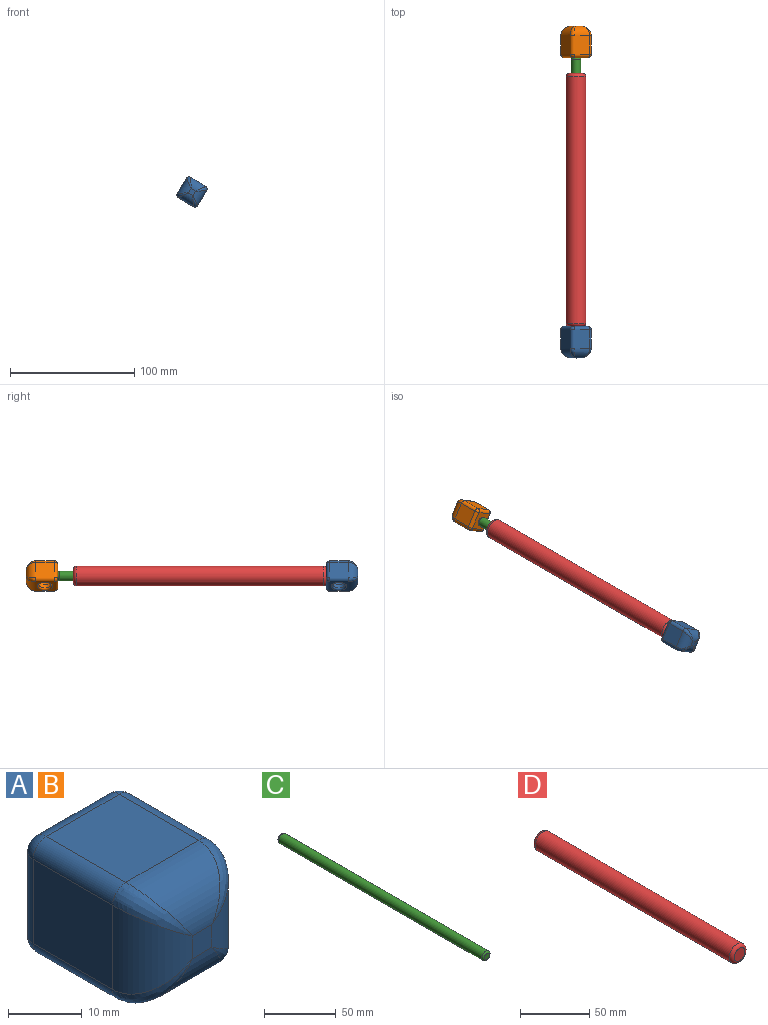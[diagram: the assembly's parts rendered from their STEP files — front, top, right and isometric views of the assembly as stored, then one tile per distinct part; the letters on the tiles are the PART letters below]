
ASSEMBLY  parts=4 mates=6
PART A: 29 faces, bbox 19.1x25.4x19.1 mm
  f0: plane 15.24x13.97mm, normal (0,0,-1), area 212.9mm2, adj f11,f15,f17,f23
  f1: plane 15.24x13.97mm, normal (1,0,0), area 86.2mm2, adj f8,f14,f17,f24,f27
  f2: plane 15.24x13.97mm, normal (0,0,1), area 212.9mm2, adj f6,f8,f9,f20
  f3: plane 15.24x13.97mm, normal (-1,0,0), area 212.9mm2, adj f6,f10,f11,f19
  f4: plane 3.81x3.81mm, normal (0,-1,0), area 14.5mm2, adj f19,f20,f23,f24
  f5: plane 13.97x13.97mm, normal (0,1,0), area 195.2mm2, adj f9,f10,f14,f15
  f6: cylinder r=2.54mm len=15.24mm, axis (0,-1,0), area 60.8mm2, adj f2,f3,f7,f18
  f7: sphere r=2.54mm, area 10.1mm2, adj f6,f9,f10
  f8: cylinder r=2.54mm len=15.24mm, axis (0,1,0), area 60.8mm2, adj f1,f2,f12,f22
  f9: cylinder r=2.54mm len=13.97mm, axis (-1,0,0), area 55.7mm2, adj f2,f5,f7,f12
  f10: cylinder r=2.54mm len=13.97mm, axis (0,0,-1), area 55.7mm2, adj f3,f5,f7,f13
  f11: cylinder r=2.54mm len=15.24mm, axis (0,1,0), area 60.8mm2, adj f0,f3,f13,f21
  f12: sphere r=2.54mm, area 10.1mm2, adj f8,f9,f14
  f13: sphere r=2.54mm, area 10.1mm2, adj f10,f11,f15
  f14: cylinder r=2.54mm len=13.97mm, axis (0,0,1), area 55.7mm2, adj f1,f5,f12,f16
  f15: cylinder r=2.54mm len=13.97mm, axis (1,0,0), area 55.7mm2, adj f0,f5,f13,f16
  f16: sphere r=2.54mm, area 10.1mm2, adj f14,f15,f17
  f17: cylinder r=2.54mm len=15.24mm, axis (0,-1,0), area 60.8mm2, adj f0,f1,f16,f25
  f18: bspline ~8.94x7.62mm, area 32.5mm2, adj f6,f19,f20
  f19: cylinder r=7.62mm len=13.97mm, axis (0,0,1), area 123mm2, adj f3,f4,f18,f21
  f20: cylinder r=7.62mm len=13.97mm, axis (1,0,0), area 123mm2, adj f2,f4,f18,f22
  f21: bspline ~8.94x7.62mm, area 32.5mm2, adj f11,f19,f23
  f22: bspline ~8.94x7.62mm, area 32.5mm2, adj f8,f20,f24
  f23: cylinder r=7.62mm len=13.97mm, axis (-1,0,0), area 123mm2, adj f0,f4,f21,f25
  f24: cylinder r=7.62mm len=13.97mm, axis (0,0,-1), area 123mm2, adj f1,f4,f22,f25
  f25: bspline ~8.94x7.62mm, area 32.5mm2, adj f17,f23,f24
  f26: cylinder r=5.08mm len=10.16mm, axis (1,0,0), area 101.3mm2, adj f27,f28
  f27: torus R=6.35mm, axis (-1,0,0), area 69.5mm2, adj f1,f26
  f28: sphere r=5.08mm, area 162.1mm2, adj f26
PART B: same geometry as A
PART C: 5 faces, bbox 8.2x203.2x8.2 mm
  f0: cylinder r=3.81mm len=200.66mm, axis (0,-1,0), area 4803.6mm2, adj f3,f4
  f1: plane 5.08x5.08mm, normal (0,1,0), area 20.3mm2, adj f4
  f2: plane 5.08x5.08mm, normal (0,-1,0), area 20.3mm2, adj f3
  f3: torus R=2.54mm, axis (0,-1,0), area 42mm2, adj f0,f2
  f4: torus R=2.54mm, axis (0,-1,0), area 42mm2, adj f0,f1
PART D: 5 faces, bbox 17.3x203.2x17.3 mm
  f0: cylinder r=8mm len=198.12mm, axis (0,1,0), area 9959.8mm2, adj f3,f4
  f1: plane 10.92x10.92mm, normal (0,-1,0), area 93.7mm2, adj f4
  f2: plane 10.92x10.92mm, normal (0,1,0), area 93.7mm2, adj f3
  f3: torus R=5.46mm, axis (0,-1,0), area 177.4mm2, adj f0,f2
  f4: torus R=5.46mm, axis (0,-1,0), area 177.4mm2, adj f0,f1
PLACE A rot(axis=(0,1,0),121.4deg) t=(-1.52,97.32,0)mm
PLACE B rot(axis=(-0.49,0,0.87),180deg) t=(-1.52,-93.18,0)mm
PLACE C t=(-1.52,-93.18,0)mm
PLACE D t=(-1.52,97.32,0)mm fixed
MATE planar B.f5 <-> C.f0  axis (0,-1,0) through (-1.52,110.02,0)mm
MATE cylindrical B.f5 <-> C.f0  axis (0,-1,0) through (-1.52,110.02,0)mm
MATE planar B.f2 <-> A.f0  axis (-0.85,0,0.52) through (-9.65,120.18,4.96)mm
MATE cylindrical C.f0 <-> D.f0  axis (0,-1,0) through (-1.52,-93.18,0)mm
MATE cylindrical A.f5 <-> D.f0  axis (0,1,0) through (-1.52,-105.88,0)mm
MATE planar A.f5 <-> D.f0  axis (0,1,0) through (-1.52,-105.88,0)mm
